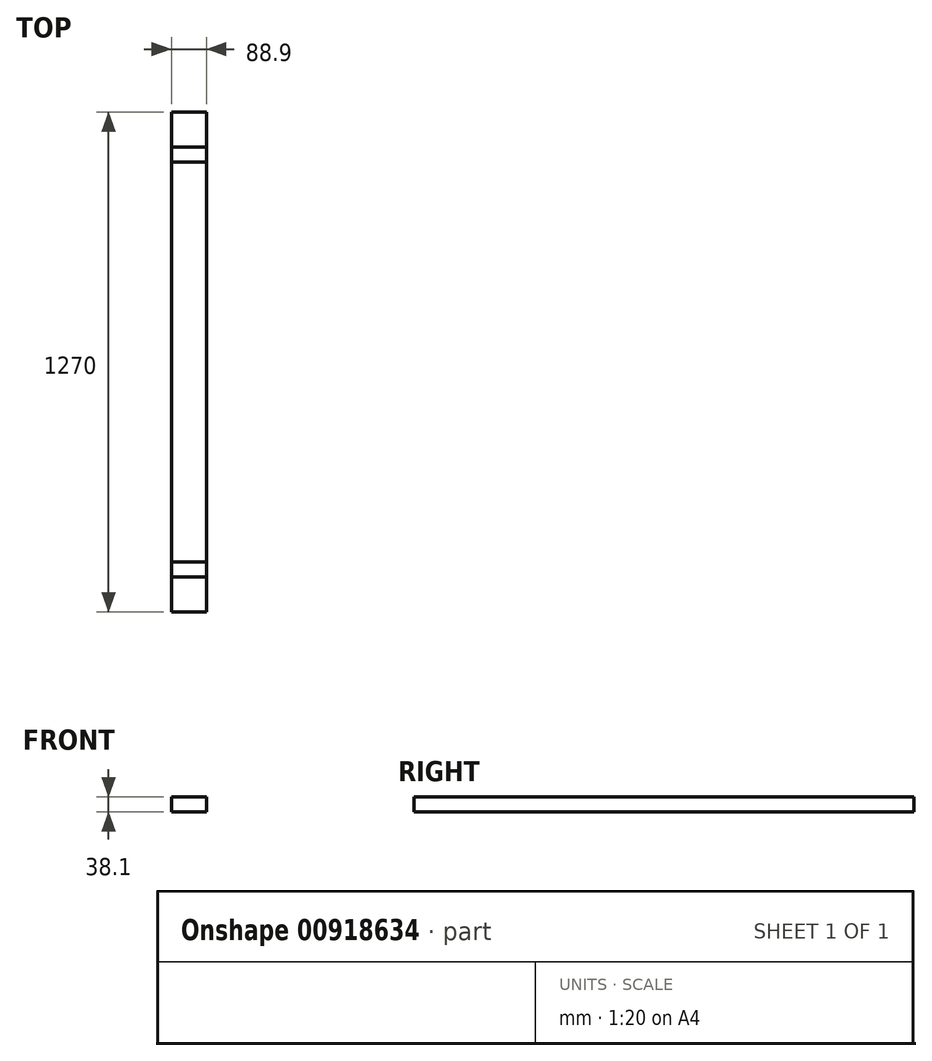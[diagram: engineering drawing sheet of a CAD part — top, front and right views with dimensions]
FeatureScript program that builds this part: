
annotation { "Feature Type Name" : "Feature", "Feature Type Description" : "" }
export const myFeature = defineFeature(function(context is Context, id is Id, definition is map)
    precondition{}
    {
        {
            var Q0;
            Q0=qCreatedBy(makeId("Front.planeOp"),FACE);
            var sketch = newSketch(context, id + "F0", { "sketchPlane" : qUnion([Q0])});
            skLineSegment(sketch, "E0.bottom", {"start": v(-44.45, 19.05) * mm, "end": v(44.45, 19.05) * mm});
            skLineSegment(sketch, "E0.top", {"start": v(-44.45, -19.05) * mm, "end": v(44.45, -19.05) * mm});
            skLineSegment(sketch, "E0.left", {"start": v(-44.45, 19.05) * mm, "end": v(-44.45, -19.05) * mm});
            skLineSegment(sketch, "E0.right", {"start": v(44.45, 19.05) * mm, "end": v(44.45, -19.05) * mm});
            skLineSegment(sketch, "E1", {"start": v(-44.45, 19.05) * mm, "end": v(44.45, -19.05) * mm, "construction": true});
            skSolve(sketch);
        }
        {
            var Q0;
            Q0=makeQuery(id+"F0.imprint","IMPRINT",FACE,{"disambiguationData":[TD([[makeQuery(id+"F0.imprint","IMPRINT",EDGE,{"derivedFrom":sQuery(id+"F0.wireOp",EDGE,"E0.bottom")}),-1.0]])]});
            extrude(context, id + "F1", {"entities" : qUnion([Q0]), "depth" : 1270 * mm, "offsetDistance" : 25.4 * mm, "symmetric" : true});
        }
        {
            var Q0;
            Q0=makeQuery(id+"F1.opExtrude","SWEPT_FACE",FACE,{"disambiguationData":[OSD([sQuery(id+"F0.wireOp",EDGE,"E0.bottom")])]});
            var sketch = newSketch(context, id + "F2", { "sketchPlane" : qUnion([Q0])});
            skLineSegment(sketch, "E2.bottom", {"start": v(-44.45, 546.1) * mm, "end": v(44.45, 546.1) * mm});
            skLineSegment(sketch, "E2.top", {"start": v(-44.45, 508) * mm, "end": v(44.45, 508) * mm});
            skLineSegment(sketch, "E2.left", {"start": v(-44.45, 546.1) * mm, "end": v(-44.45, 508) * mm});
            skLineSegment(sketch, "E2.right", {"start": v(44.45, 546.1) * mm, "end": v(44.45, 508) * mm});
            skLineSegment(sketch, "E3.bottom", {"start": v(-44.45, -508) * mm, "end": v(44.45, -508) * mm});
            skLineSegment(sketch, "E3.top", {"start": v(-44.45, -546.1) * mm, "end": v(44.45, -546.1) * mm});
            skLineSegment(sketch, "E3.left", {"start": v(-44.45, -508) * mm, "end": v(-44.45, -546.1) * mm});
            skLineSegment(sketch, "E3.right", {"start": v(44.45, -508) * mm, "end": v(44.45, -546.1) * mm});
            skLineSegment(sketch, "E4", {"start": v(0, 508) * mm, "end": v(0, -508) * mm, "construction": true});
            skPoint(sketch, "E5", {"position": v(0, 0) * mm});
            skSolve(sketch);
        }
        {
            var Q0;
            Q0=makeQuery(id+"F2.imprint","IMPRINT",FACE,{"disambiguationData":[TD([[makeQuery(id+"F2.imprint","IMPRINT",EDGE,{"derivedFrom":sQuery(id+"F2.wireOp",EDGE,"E2.bottom")}),-1.0]])]});
            var Q1;
            Q1=makeQuery(id+"F2.imprint","IMPRINT",FACE,{"disambiguationData":[TD([[makeQuery(id+"F2.imprint","IMPRINT",EDGE,{"derivedFrom":sQuery(id+"F2.wireOp",EDGE,"E3.bottom")}),-1.0]])]});
            extrude(context, id + "F3", {"entities" : qUnion([Q0, Q1]), "operationType" : NewBodyOperationType.REMOVE, "oppositeDirection" : true, "depth" : 3 / 101.6 * mm, "offsetDistance" : 25.4 * mm});
        }
    });
